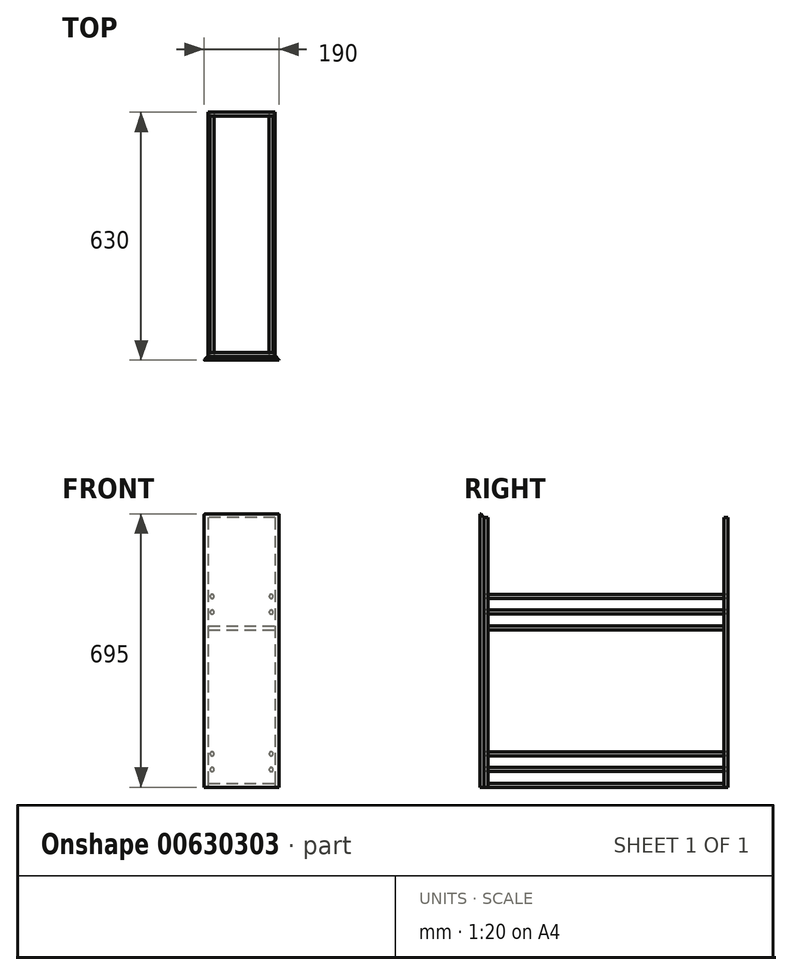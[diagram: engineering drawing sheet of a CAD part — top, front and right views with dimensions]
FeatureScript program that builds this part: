
annotation { "Feature Type Name" : "Feature", "Feature Type Description" : "" }
export const myFeature = defineFeature(function(context is Context, id is Id, definition is map)
    precondition{}
    {
        {
            var Q0;
            Q0=qCreatedBy(makeId("Top.planeOp"),FACE);
            var sketch = newSketch(context, id + "F0", { "sketchPlane" : qUnion([Q0])});
            skLineSegment(sketch, "E0.bottom", {"start": v(-85, 300) * mm, "end": v(85, 300) * mm});
            skLineSegment(sketch, "E0.top", {"start": v(-85, -300) * mm, "end": v(85, -300) * mm});
            skLineSegment(sketch, "E0.left", {"start": v(-85, 300) * mm, "end": v(-85, -300) * mm});
            skLineSegment(sketch, "E0.right", {"start": v(85, 300) * mm, "end": v(85, -300) * mm});
            skPoint(sketch, "E0.middle", {"position": v(0, 0) * mm});
            skSolve(sketch);
        }
        {
            var Q0;
            Q0 = qSketchRegion(id + "F0", true);
            extrude(context, id + "F1", {"entities" : qUnion([Q0]), "depth" : 10 * mm, "offsetDistance" : 25 * mm});
        }
        {
            var Q0;
            Q0=qCreatedBy(makeId("Top.planeOp"),FACE);
            var Q1;
            Q1 = qBodyType(qCreatedBy(id + "F3" ,EDGE), BodyType.WIRE);
            cPlane(context, id + "F2", {"entities" : qUnion([Q0, Q1]), "cplaneType" : CPlaneType.OFFSET, "offset" : 400 * mm, "width" : 150 * mm, "height" : 150 * mm});
        }
        {
            var Q0;
            Q0=qCreatedBy(id+"F2.planeOp",FACE);
            var sketch = newSketch(context, id + "F3", { "sketchPlane" : qUnion([Q0])});
            skLineSegment(sketch, "E1.bottom", {"start": v(-85, 300) * mm, "end": v(85, 300) * mm});
            skLineSegment(sketch, "E1.top", {"start": v(-85, -300) * mm, "end": v(85, -300) * mm});
            skLineSegment(sketch, "E1.left", {"start": v(-85, 300) * mm, "end": v(-85, -300) * mm});
            skLineSegment(sketch, "E1.right", {"start": v(85, 300) * mm, "end": v(85, -300) * mm});
            skPoint(sketch, "E1.middle", {"position": v(0, 0) * mm});
            skSolve(sketch);
        }
        {
            var Q0;
            Q0 = qSketchRegion(id + "F3", true);
            extrude(context, id + "F4", {"entities" : qUnion([Q0]), "depth" : 10 * mm, "offsetDistance" : 25 * mm});
        }
        {
            var Q0;
            Q0=qCreatedBy(makeId("Top.planeOp"),FACE);
            var sketch = newSketch(context, id + "F5", { "sketchPlane" : qUnion([Q0])});
            skLineSegment(sketch, "E2.bottom", {"start": v(85, 300) * mm, "end": v(-85, 300) * mm});
            skLineSegment(sketch, "E2.top", {"start": v(85, 310) * mm, "end": v(-85, 310) * mm});
            skLineSegment(sketch, "E2.left", {"start": v(85, 300) * mm, "end": v(85, 310) * mm});
            skLineSegment(sketch, "E2.right", {"start": v(-85, 300) * mm, "end": v(-85, 310) * mm});
            skLineSegment(sketch, "E3.MirrorCS", {"start": v(85, -310) * mm, "end": v(-85, -310) * mm});
            skLineSegment(sketch, "E4.MirrorCS", {"start": v(-85, -300) * mm, "end": v(-85, -310) * mm});
            skLineSegment(sketch, "E5.MirrorCS", {"start": v(85, -300) * mm, "end": v(-85, -300) * mm});
            skLineSegment(sketch, "E6.MirrorCS", {"start": v(85, -300) * mm, "end": v(85, -310) * mm});
            skSolve(sketch);
        }
        {
            var Q0;
            Q0 = qSketchRegion(id + "F5", true);
            extrude(context, id + "F6", {"entities" : qUnion([Q0]), "depth" : 685 * mm, "offsetDistance" : 25 * mm});
        }
        {
            var Q0;
            Q0=qCreatedBy(makeId("Front.planeOp"),FACE);
            cPlane(context, id + "F7", {"entities" : qUnion([Q0]), "cplaneType" : CPlaneType.OFFSET, "offset" : 310 * mm, "width" : 150 * mm, "height" : 150 * mm});
        }
        {
            var Q0;
            Q0=qCreatedBy(id+"F7.planeOp",FACE);
            var sketch = newSketch(context, id + "F8", { "sketchPlane" : qUnion([Q0])});
            skCircle(sketch, "E7", {"center": v(-75, 45) * mm, "radius": 5 * mm});
            skCircle(sketch, "E8", {"center": v(-75, 85) * mm, "radius": 5 * mm});
            skCircle(sketch, "E9.MirrorC", {"center": v(75, 45) * mm, "radius": 5 * mm});
            skCircle(sketch, "E10.MirrorC", {"center": v(75, 85) * mm, "radius": 5 * mm});
            skCircle(sketch, "E11", {"center": v(-75, 445) * mm, "radius": 5 * mm});
            skCircle(sketch, "E12", {"center": v(-75, 485) * mm, "radius": 5 * mm});
            skPoint(sketch, "E13", {"position": v(-85, 410) * mm});
            skCircle(sketch, "E14.MirrorC", {"center": v(75, 485) * mm, "radius": 5 * mm});
            skCircle(sketch, "E15.MirrorC", {"center": v(75, 445) * mm, "radius": 5 * mm});
            skPoint(sketch, "E16", {"position": v(-85, 10) * mm});
            skSolve(sketch);
        }
        {
            var Q0;
            Q0 = qSketchRegion(id + "F8", true);
            extrude(context, id + "F9", {"entities" : qUnion([Q0]), "oppositeDirection" : true, "depth" : 620 * mm, "offsetDistance" : 25 * mm});
        }
        {
            var Q0;
            Q0=qCreatedBy(id+"F7.planeOp",FACE);
            var sketch = newSketch(context, id + "F10", { "sketchPlane" : qUnion([Q0])});
            skLineSegment(sketch, "E17.bottom", {"start": v(95, 0) * mm, "end": v(-95, 0) * mm});
            skLineSegment(sketch, "E17.top", {"start": v(95, 695) * mm, "end": v(-95, 695) * mm});
            skLineSegment(sketch, "E17.left", {"start": v(95, 0) * mm, "end": v(95, 695) * mm});
            skLineSegment(sketch, "E17.right", {"start": v(-95, 0) * mm, "end": v(-95, 695) * mm});
            skSolve(sketch);
        }
        {
            var Q0;
            Q0 = qSketchRegion(id + "F10", true);
            extrude(context, id + "F11", {"entities" : qUnion([Q0]), "depth" : 10 * mm, "offsetDistance" : 25 * mm});
        }
        {
            var Q0;
            Q0=makeQuery(id+"F11.opExtrude","CAP_EDGE",EDGE,{"disambiguationData":[OSD([sQuery(id+"F10.wireOp",EDGE,"E17.top")])],"isStart":true});
            var Q1;
            Q1=makeQuery(id+"F11.opExtrude","CAP_EDGE",EDGE,{"disambiguationData":[OSD([sQuery(id+"F10.wireOp",EDGE,"E17.left")])],"isStart":true});
            var Q2;
            Q2=makeQuery(id+"F11.opExtrude","CAP_EDGE",EDGE,{"disambiguationData":[OSD([sQuery(id+"F10.wireOp",EDGE,"E17.right")])],"isStart":true});
            chamfer(context, id + "F12", {"entities" : qUnion([Q0, Q1, Q2]), "width" : 9 * mm, "tangentPropagation" : true});
        }
        {
            var Q0;
            {var subQ0=sQuery(id+"F10.wireOp",EDGE,"E17.right");Q0=makeQuery(id+"F12.opChamfer","BLEND_EDGE",EDGE,{"blendedFrom":[makeQuery(id+"F11.opExtrude","CAP_EDGE",EDGE,{"disambiguationData":[OSD([subQ0])],"isStart":true}),makeQuery(id+"F11.opExtrude","SWEPT_FACE",FACE,{"disambiguationData":[OSD([subQ0])]})],"blendedInto":[makeQuery(id+"F11.opExtrude","SWEPT_FACE",FACE,{"disambiguationData":[OSD([subQ0])]})]});}
            var Q1;
            {var subQ0=sQuery(id+"F10.wireOp",EDGE,"E17.right");Q1=makeQuery(id+"F12.opChamfer","BLEND_EDGE",EDGE,{"blendedFrom":[makeQuery(id+"F11.opExtrude","CAP_EDGE",EDGE,{"disambiguationData":[OSD([subQ0])],"isStart":true}),makeQuery(id+"F11.opExtrude","CAP_FACE",FACE,{"disambiguationData":[OSD([sQuery(id+"F10.wireOp",EDGE,"E17.bottom"),sQuery(id+"F10.wireOp",EDGE,"E17.top"),sQuery(id+"F10.wireOp",EDGE,"E17.left"),subQ0])],"isStart":true})],"blendedInto":[makeQuery(id+"F11.opExtrude","CAP_FACE",FACE,{"disambiguationData":[OSD([sQuery(id+"F10.wireOp",EDGE,"E17.bottom"),sQuery(id+"F10.wireOp",EDGE,"E17.top"),sQuery(id+"F10.wireOp",EDGE,"E17.left"),subQ0])],"isStart":true})]});}
            var Q2;
            {var subQ0=sQuery(id+"F10.wireOp",EDGE,"E17.left");Q2=makeQuery(id+"F12.opChamfer","BLEND_EDGE",EDGE,{"blendedFrom":[makeQuery(id+"F11.opExtrude","CAP_EDGE",EDGE,{"disambiguationData":[OSD([subQ0])],"isStart":true}),makeQuery(id+"F11.opExtrude","CAP_FACE",FACE,{"disambiguationData":[OSD([sQuery(id+"F10.wireOp",EDGE,"E17.bottom"),sQuery(id+"F10.wireOp",EDGE,"E17.top"),subQ0,sQuery(id+"F10.wireOp",EDGE,"E17.right")])],"isStart":true})],"blendedInto":[makeQuery(id+"F11.opExtrude","CAP_FACE",FACE,{"disambiguationData":[OSD([sQuery(id+"F10.wireOp",EDGE,"E17.bottom"),sQuery(id+"F10.wireOp",EDGE,"E17.top"),subQ0,sQuery(id+"F10.wireOp",EDGE,"E17.right")])],"isStart":true})]});}
            var Q3;
            {var subQ0=sQuery(id+"F10.wireOp",EDGE,"E17.left");Q3=makeQuery(id+"F12.opChamfer","BLEND_EDGE",EDGE,{"blendedFrom":[makeQuery(id+"F11.opExtrude","CAP_EDGE",EDGE,{"disambiguationData":[OSD([subQ0])],"isStart":true}),makeQuery(id+"F11.opExtrude","SWEPT_FACE",FACE,{"disambiguationData":[OSD([subQ0])]})],"blendedInto":[makeQuery(id+"F11.opExtrude","SWEPT_FACE",FACE,{"disambiguationData":[OSD([subQ0])]})]});}
            fillet(context, id + "F13", {"entities" : qUnion([Q0, Q1, Q2, Q3]), "radius" : 3 * mm, "tangentPropagation" : true, "allowEdgeOverflow" : false});
        }
        {
            var Q0;
            {var subQ0=sQuery(id+"F10.wireOp",EDGE,"E17.top");Q0=makeQuery(id+"F12.opChamfer","BLEND_EDGE",EDGE,{"blendedFrom":[makeQuery(id+"F11.opExtrude","CAP_EDGE",EDGE,{"disambiguationData":[OSD([subQ0])],"isStart":true}),makeQuery(id+"F11.opExtrude","SWEPT_FACE",FACE,{"disambiguationData":[OSD([subQ0])]})],"blendedInto":[makeQuery(id+"F11.opExtrude","SWEPT_FACE",FACE,{"disambiguationData":[OSD([subQ0])]})]});}
            var Q1;
            {var subQ0=sQuery(id+"F10.wireOp",EDGE,"E17.top");Q1=makeQuery(id+"F12.opChamfer","BLEND_EDGE",EDGE,{"blendedFrom":[makeQuery(id+"F11.opExtrude","CAP_EDGE",EDGE,{"disambiguationData":[OSD([subQ0])],"isStart":true}),makeQuery(id+"F11.opExtrude","CAP_FACE",FACE,{"disambiguationData":[OSD([sQuery(id+"F10.wireOp",EDGE,"E17.bottom"),subQ0,sQuery(id+"F10.wireOp",EDGE,"E17.left"),sQuery(id+"F10.wireOp",EDGE,"E17.right")])],"isStart":true})],"blendedInto":[makeQuery(id+"F11.opExtrude","CAP_FACE",FACE,{"disambiguationData":[OSD([sQuery(id+"F10.wireOp",EDGE,"E17.bottom"),subQ0,sQuery(id+"F10.wireOp",EDGE,"E17.left"),sQuery(id+"F10.wireOp",EDGE,"E17.right")])],"isStart":true})]});}
            fillet(context, id + "F14", {"entities" : qUnion([Q0, Q1]), "radius" : 3 * mm, "tangentPropagation" : true, "allowEdgeOverflow" : false});
        }
    });
